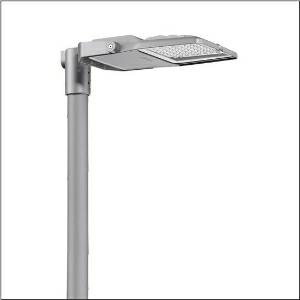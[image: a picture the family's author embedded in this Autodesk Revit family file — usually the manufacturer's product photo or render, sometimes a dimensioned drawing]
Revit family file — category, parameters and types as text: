
# Revit family: floodlight_fl_21_mini___pl43_5xa7771b4a3a_4487
name_source: partatom
category: Lighting Fixtures
units: mm (PartAtom-declared; Revit-internal decimal feet)

## family parameters
Cut with Voids When Loaded = No
Host = Face
Light Source = No
Part Type = Normal
Room Calculation Point = No
Round Connector Dimension = Use Diameter
Shared = No

## types (1)
- --- (1 x LED, 6660 lm, 45.5 W, 4000K)
    Apparent Load = 46 VA
    CIE Flux Codes = 27 78 99 100 100
    Color Rendering = 70
    Color Temperature = 4000K
    Default Elevation = 1800 mm
    Description = Floodlight FL 21 mini, floodlight, primary light control with lens, of PMMA, primary optical cover: protective disc, of toughened safety glass, transparent, light distribution: PL43, light emission: direct distribution, installation type: surface-mounted, LED, High Power LED, rated luminous flux: 6.660lm, luminous efficacy: 146lm/W, light colour: 740, colour temperature: 4000K, control gear: ECG iQ, control: Auto-Match, Temp-Guard, Lumen-Switch, Night-Set, Smart-Wire, Light-Fading, Desk-Remote (wireless, voltage-free reading and setting of iQ features in the workshop via application-optimized NFC function/RFID function), optimised constant luminous flux control (CLO 2.0), with terminal, 6-pole, mains connection: 220..240V, AC, 50/60Hz, start of lifetime: 46W, end of lifetime: 48W, reduction: 22W, luminaire housing, of diecast aluminium, powder-coated, Siteco® metallic grey (DB 702S), corrosivity category C5 according to DIN EN ISO 12944, mast bracket, of steel, galvanised, powder-coated, Siteco® metallic grey (DB 702S), protection rating (complete): IP66, insulation class (complete): insulation class II (safety insulation), certification: CE, ENEC, VDE, protection symbol: D, impact resistance: IK08, permissible operating ambient temperature: -40..+40°C, permissible operating ambient temperature for outdoor applications: -40..+50°C, standard: DIN EN 12944, packaging unit: 1 piece

Light Distribution: PL43
    Height = 70 mm
    Lamp = 1 x LED
    Lamp Light Flux = 6660 lm
    Lamp Power = 45.5 W
    Lamp count = 1
    Length = 485 mm
    Luminous efficacy = 146 lm/W
    Manufacturer = Siteco
    ModVariant = No
    Model = 5XA7771B4A3A
    Number of Poles = 1
    OnlyDefault = Yes
    Power Factor = 1
    Product Name = Floodlight FL 21 mini | PL43
    Product group = floodlight | pylon top
    ProductGroupID = 6101
    Protection Class = Protection class II
    Protection Degree = IP 66
    RLX_Detail_Level = 1
    RlxData = <blob elided: 100965 chars, md5=d9e802f8>
    Socket = socket
    Standby Power = 0 W
    System Light Flux = 6660 lm
    System Power = 46 W
    Type Comments = factory setting: luminous flux: 100 % | dim-lin: 254 | 463 mA
    Type Image = l_1007125.jpg
    URL = http://relux.com
    VarID = @adj_074085
    Voltage = 0 V
    Weight = 0.00 kg
    Width = 337 mm

## geometry (parser evidence)
native form markers: Blend x4, Sweep x13
no freeform markers — native parametric forms only
